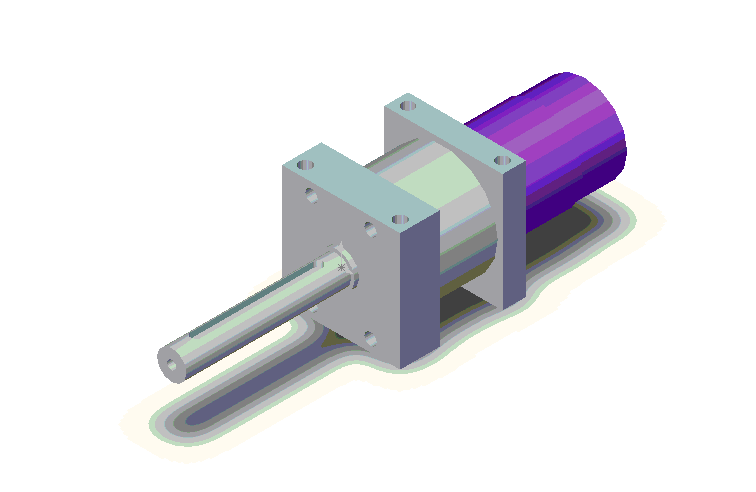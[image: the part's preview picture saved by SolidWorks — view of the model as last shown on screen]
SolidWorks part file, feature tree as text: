
SOLIDWORKS PART (.sldprt)
format: sldprt  version: not decoded by parser v0  size: 541,184 bytes
history: native  units: mm
features: sketch x14, extrude x7, cut_extrude x7, plane x2 (+8 scaffold rows collapsed)
feature tree (38):
  scaffold x8  (default folders/planes/origin — collapsed)
  sketch  "Sketch1"  dims[D13=4.0mm D14=4.0mm D15=4.0mm D16=4.0mm D1=19.05mm D2=38.1mm D3=19.05mm D4=38.1mm D5=9.525mm D6=9.53mm D7=9.53mm D8=9.53mm D9=3.81mm D10=3.81mm D11=34.29mm D12=34.29mm]
  extrude  "Base-Extrude"  Depth=12.7mm
  sketch  "Sketch2"  dims[D1=9.525mm]
  extrude  "Boss-Extrude1"  Depth=54.61mm
  plane  "Plane1"
  sketch  "Sketch3"  dims[D1=3.175mm D2=3.175mm D3=7.62mm D4=39.37mm]
  plane  "Plane2"  Offset=2.7625mm
  cut_extrude  "Cut-Extrude3"  [1 undecoded]
  sketch  "Sketch4"  dims[D1=3.0mm]
  cut_extrude  "Cut-Extrude4"  Depth=9.525mm
  sketch  "Sketch5"
  extrude  "Boss-Extrude2"  Depth=1.5mm
  sketch  "Sketch6"  dims[D1=4.0mm D2=4.0mm D3=3.81mm D4=34.29mm D5=3.81mm D6=3.81mm]
  cut_extrude  "Cut-Extrude5"  Depth=9.5mm
  sketch  "Sketch7"  dims[D1=15.24mm]
  cut_extrude  "Cut-Extrude6"  Depth=9.5mm
  sketch  "Sketch8"  dims[D1=35.0mm]
  extrude  "Boss-Extrude3"  Depth=20.32mm
  sketch  "Sketch9"
  extrude  "Boss-Extrude4"  Depth=7.62mm
  sketch  "Sketch11"  dims[D7=4.0mm D8=4.0mm D9=4.0mm D10=4.0mm D14=4.0mm D15=4.0mm D17=4.0mm D18=4.0mm D1=9.525mm D2=9.525mm D3=28.575mm D4=28.575mm D5=3.81mm D6=34.29mm D11=3.81mm D12=9.53mm D13=28.58mm D16=34.29mm]
  cut_extrude  "Cut-Extrude7"  Depth=9.525mm
  sketch  "Sketch12"  dims[c1.D3=4.0mm c1.D4=4.0mm c1.D1=3.81mm c1.D2=3.81mm c2.D3=3.81mm c2.D5=3.81mm]
  cut_extrude  "Cut-Extrude8"  Depth=9.525mm
  sketch  "Sketch13"
  cut_extrude  "Cut-Extrude9"  Depth=9.525mm
  sketch  "Sketch14"  dims[D1=27.7mm]
  extrude  "Boss-Extrude5"  Depth=37.8mm
  sketch  "Sketch15"  dims[D1=28.956mm]
  extrude  "Boss-Extrude6"  Depth=23mm
decode coverage: 24 of 28 modeling features carry decoded parameters
note: 1 parameter value undecoded
note: suppression state not decoded; provenance and decode notes live in map.json
